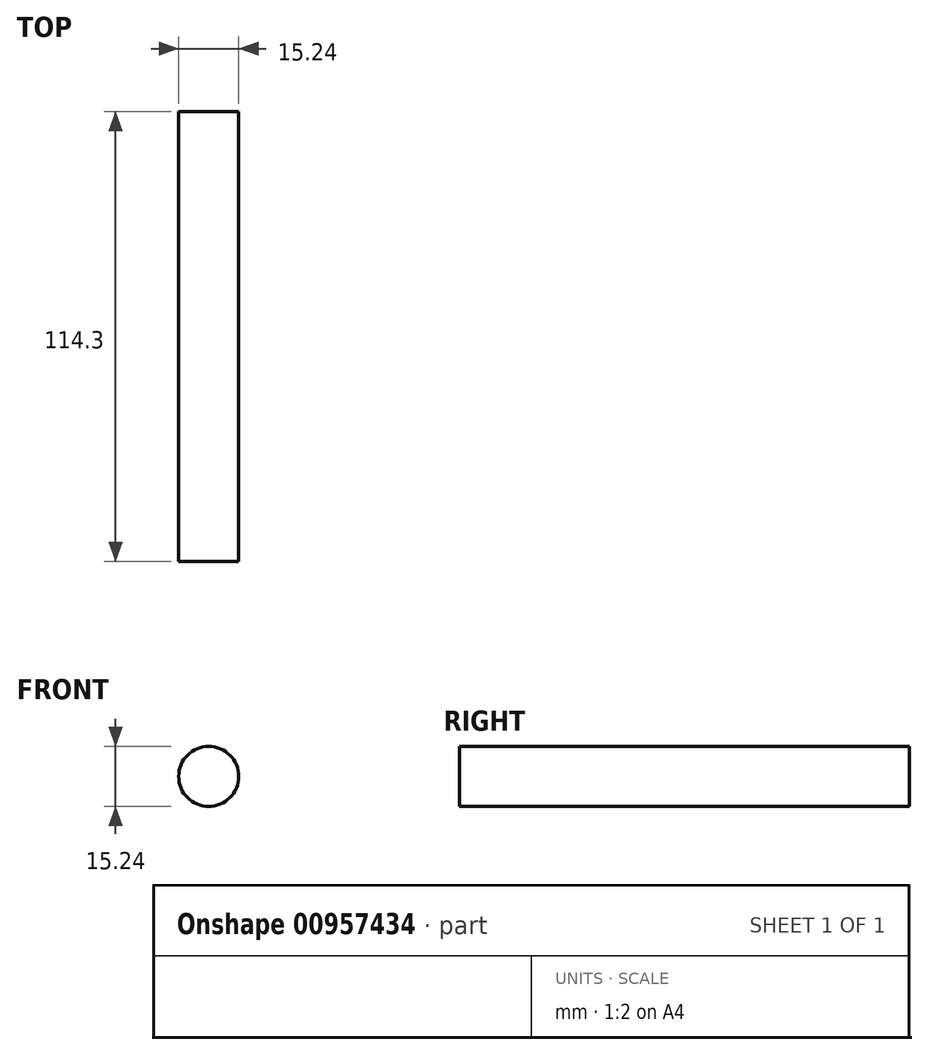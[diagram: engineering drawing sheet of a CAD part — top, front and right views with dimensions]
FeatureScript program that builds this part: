
annotation { "Feature Type Name" : "Feature", "Feature Type Description" : "" }
export const myFeature = defineFeature(function(context is Context, id is Id, definition is map)
    precondition{}
    {
        {
            var Q0;
            Q0=qCreatedBy(makeId("Front.planeOp"),FACE);
            var sketch = newSketch(context, id + "F0", { "sketchPlane" : qUnion([Q0])});
            skCircle(sketch, "E0", {"center": v(-107, 23.35) * mm, "radius": 7.62 * mm});
            skSolve(sketch);
        }
        {
            var Q0;
            Q0=makeQuery(id+"F0.imprint","IMPRINT",FACE,{"disambiguationData":[TD([[makeQuery(id+"F0.imprint","IMPRINT",EDGE,{"derivedFrom":sQuery(id+"F0.wireOp",EDGE,"E0")}),1.0]])]});
            extrude(context, id + "F1", {"entities" : qUnion([Q0]), "depth" : 114.3 * mm, "offsetDistance" : 25.4 * mm});
        }
    });
